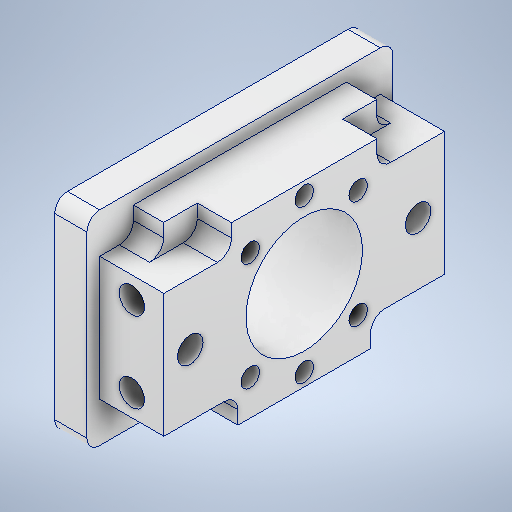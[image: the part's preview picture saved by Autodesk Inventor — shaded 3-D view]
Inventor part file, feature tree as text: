
AUTODESK INVENTOR PART (.ipt)
format: ipt  version: 2025.2 (Build 292293000, 293)  size: 392,704 bytes
history: native  units: mm
features: extrude x6, fillet x2, plane x1, mirror x1
ambient origin geometry x8: Origin, YZ Plane, XZ Plane, XY Plane, X Axis, Y Axis, Z Axis, Center Point
bodies: Solid1 (feature_tree)
feature tree (10):
  extrude  "Extrusion1"  Depth=50.8mm
  extrude  "Extrusion2"  Depth=76.2mm
  plane  "Work Plane1"
  mirror  "Mirror1"
  extrude  "Extrusion4"  Depth=3.175mm
  extrude  "Extrusion5"  Depth=26.5mm
  fillet  "Fillet1"  Radius=10.0mm
  extrude  "Extrusion3"  Depth=16.0mm TaperAngle=0.0deg
  extrude  "Extrusion6"  Depth=16.0mm
  fillet  "Fillet2"  Radius=50.8mm
